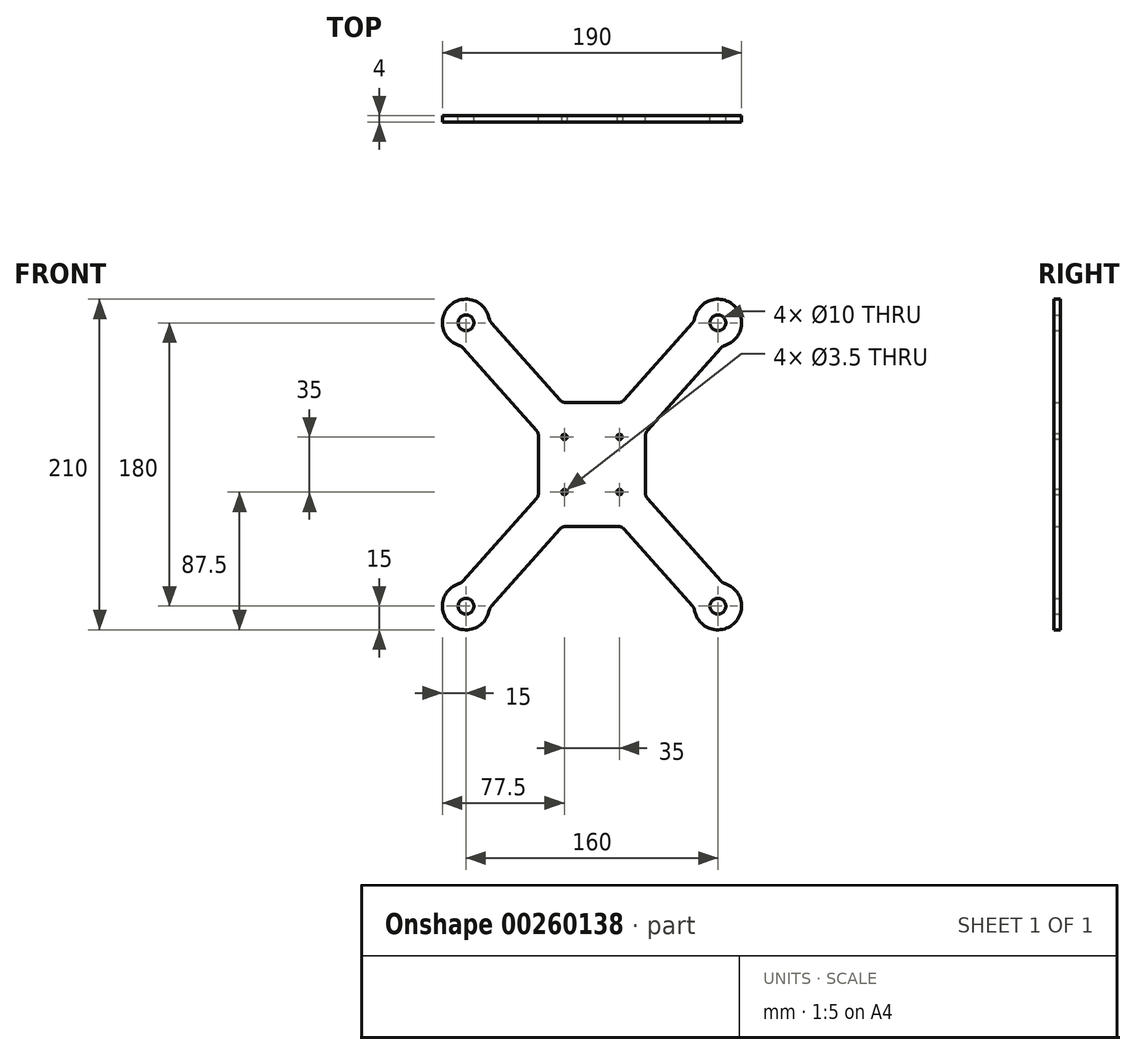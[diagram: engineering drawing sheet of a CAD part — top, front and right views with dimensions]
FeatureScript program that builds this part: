
annotation { "Feature Type Name" : "Feature", "Feature Type Description" : "" }
export const myFeature = defineFeature(function(context is Context, id is Id, definition is map)
    precondition{}
    {
        {
            var Q0;
            Q0=qCreatedBy(makeId("Front.planeOp"),FACE);
            var sketch = newSketch(context, id + "F0", { "sketchPlane" : qUnion([Q0])});
            skLineSegment(sketch, "E0", {"start": v(0, -138.98) * mm, "end": v(0, 18.06) * mm, "construction": true});
            skLineSegment(sketch, "E1.bottom", {"start": v(0, 90) * mm, "end": v(-80, 90) * mm, "construction": true});
            skLineSegment(sketch, "E1.top", {"start": v(0, -90) * mm, "end": v(-80, -90) * mm, "construction": true});
            skLineSegment(sketch, "E1.left", {"start": v(0, 90) * mm, "end": v(0, -90) * mm, "construction": true});
            skLineSegment(sketch, "E1.right", {"start": v(-80, 90) * mm, "end": v(-80, -90) * mm, "construction": true});
            skArc(sketch, "E2", {"start": v(-65.05, 91.25) * mm, "mid": v(-89.97, 101.21) * mm, "end": v(-82.99, 75.3) * mm});
            skArc(sketch, "E3", {"start": v(-82.99, -75.3) * mm, "mid": v(-89.97, -101.21) * mm, "end": v(-65.05, -91.25) * mm});
            skPoint(sketch, "E4", {"position": v(-80, 0) * mm});
            skLineSegment(sketch, "E5", {"start": v(-70.03, 78.79) * mm, "end": v(0, 0) * mm, "construction": true});
            skLineSegment(sketch, "E6", {"start": v(0, 0) * mm, "end": v(-80, -90) * mm, "construction": true});
            skLineSegment(sketch, "E7.0", {"start": v(-35.26, -21.6) * mm, "end": v(-82.99, -75.3) * mm});
            skLineSegment(sketch, "E7.1", {"start": v(-82.99, 75.3) * mm, "end": v(-35.26, 21.6) * mm});
            skLineSegment(sketch, "E8.0", {"start": v(-20.45, -41.07) * mm, "end": v(-65.05, -91.25) * mm});
            skLineSegment(sketch, "E8.1", {"start": v(-65.05, 91.25) * mm, "end": v(-20.45, 41.07) * mm});
            skLineSegment(sketch, "E9.trimOffspring", {"start": v(0, 90) * mm, "end": v(0, 152.4) * mm, "construction": true});
            skLineSegment(sketch, "E10.MirrorCS", {"start": v(65.05, 91.25) * mm, "end": v(20.45, 41.07) * mm});
            skArc(sketch, "E11.MirrorC", {"start": v(65.05, 91.25) * mm, "mid": v(89.97, 101.21) * mm, "end": v(82.99, 75.3) * mm});
            skLineSegment(sketch, "E12.MirrorCS", {"start": v(82.99, 75.3) * mm, "end": v(35.26, 21.6) * mm});
            skLineSegment(sketch, "E13.MirrorCS", {"start": v(35.26, -21.6) * mm, "end": v(82.99, -75.3) * mm});
            skArc(sketch, "E14.MirrorC", {"start": v(82.99, -75.3) * mm, "mid": v(89.97, -101.21) * mm, "end": v(65.05, -91.25) * mm});
            skLineSegment(sketch, "E15.MirrorCS", {"start": v(20.45, -41.07) * mm, "end": v(65.05, -91.25) * mm});
            skLineSegment(sketch, "E16.bottom", {"start": v(-16.72, 39.4) * mm, "end": v(16.72, 39.4) * mm});
            skLineSegment(sketch, "E16.top", {"start": v(-16.72, -39.4) * mm, "end": v(16.72, -39.4) * mm});
            skLineSegment(sketch, "E16.left", {"start": v(-34, 18.29) * mm, "end": v(-34, -18.29) * mm});
            skLineSegment(sketch, "E16.right", {"start": v(34, 18.29) * mm, "end": v(34, -18.29) * mm});
            skPoint(sketch, "E16.middle", {"position": v(0, 0) * mm});
            skPoint(sketch, "E17.newPointA", {"position": v(-16.06, 0) * mm});
            skArc(sketch, "E17.filletArc", {"start": v(-34, 18.29) * mm, "mid": v(-34.33, 20.06) * mm, "end": v(-35.26, 21.6) * mm});
            skArc(sketch, "E18.filletArc", {"start": v(-35.26, -21.6) * mm, "mid": v(-34.33, -20.06) * mm, "end": v(-34, -18.29) * mm});
            skPoint(sketch, "E19.newPointA", {"position": v(-35.02, 39.4) * mm});
            skPoint(sketch, "E19.newPointB", {"position": v(0, 18.06) * mm});
            skArc(sketch, "E19.filletArc", {"start": v(-20.45, 41.07) * mm, "mid": v(-18.76, 39.83) * mm, "end": v(-16.72, 39.4) * mm});
            skPoint(sketch, "E20.newPointA", {"position": v(35.02, 39.4) * mm});
            skArc(sketch, "E20.filletArc", {"start": v(16.72, 39.4) * mm, "mid": v(18.76, 39.83) * mm, "end": v(20.45, 41.07) * mm});
            skPoint(sketch, "E21.newPointB", {"position": v(16.06, 0) * mm});
            skArc(sketch, "E21.filletArc", {"start": v(35.26, 21.6) * mm, "mid": v(34.33, 20.06) * mm, "end": v(34, 18.29) * mm});
            skArc(sketch, "E22.filletArc", {"start": v(34, -18.29) * mm, "mid": v(34.33, -20.06) * mm, "end": v(35.26, -21.6) * mm});
            skPoint(sketch, "E23.newPointA", {"position": v(35.02, -39.4) * mm});
            skPoint(sketch, "E23.newPointB", {"position": v(0, -18.06) * mm});
            skArc(sketch, "E23.filletArc", {"start": v(20.45, -41.07) * mm, "mid": v(18.76, -39.83) * mm, "end": v(16.72, -39.4) * mm});
            skPoint(sketch, "E24.newPointB", {"position": v(-35.02, -39.4) * mm});
            skArc(sketch, "E24.filletArc", {"start": v(-16.72, -39.4) * mm, "mid": v(-18.76, -39.83) * mm, "end": v(-20.45, -41.07) * mm});
            skCircle(sketch, "E25", {"center": v(80, 90) * mm, "radius": 5 * mm});
            skCircle(sketch, "E26.MirrorC", {"center": v(80, -90) * mm, "radius": 5 * mm});
            skCircle(sketch, "E27.MirrorC", {"center": v(-80, -90) * mm, "radius": 5 * mm});
            skCircle(sketch, "E28.MirrorC", {"center": v(-80, 90) * mm, "radius": 5 * mm});
            skLineSegment(sketch, "E29", {"start": v(-80, -90) * mm, "end": v(-68.79, -99.97) * mm, "construction": true});
            skLineSegment(sketch, "E30", {"start": v(-80, -90) * mm, "end": v(-79.12, -104.97) * mm, "construction": true});
            skSolve(sketch);
        }
        {
            var Q0;
            Q0 = qSketchRegion(id + "F0", true);
            extrude(context, id + "F1", {"entities" : qUnion([Q0]), "depth" : 4 * mm});
        }
        {
            var Q0;
            Q0=makeQuery(id+"F1.opExtrude","CAP_FACE",FACE,{"disambiguationData":[OSD([sQuery(id+"F0.wireOp",EDGE,"E2"),sQuery(id+"F0.wireOp",EDGE,"E3"),sQuery(id+"F0.wireOp",EDGE,"E7.0"),sQuery(id+"F0.wireOp",EDGE,"E7.1"),sQuery(id+"F0.wireOp",EDGE,"E8.0"),sQuery(id+"F0.wireOp",EDGE,"E8.1"),sQuery(id+"F0.wireOp",EDGE,"E10.MirrorCS"),sQuery(id+"F0.wireOp",EDGE,"E11.MirrorC"),sQuery(id+"F0.wireOp",EDGE,"E12.MirrorCS"),sQuery(id+"F0.wireOp",EDGE,"E13.MirrorCS"),sQuery(id+"F0.wireOp",EDGE,"E14.MirrorC"),sQuery(id+"F0.wireOp",EDGE,"E15.MirrorCS"),sQuery(id+"F0.wireOp",EDGE,"E16.bottom"),sQuery(id+"F0.wireOp",EDGE,"E16.top"),sQuery(id+"F0.wireOp",EDGE,"E16.left"),sQuery(id+"F0.wireOp",EDGE,"E16.right"),sQuery(id+"F0.wireOp",EDGE,"E17.filletArc"),sQuery(id+"F0.wireOp",EDGE,"E18.filletArc"),sQuery(id+"F0.wireOp",EDGE,"E19.filletArc"),sQuery(id+"F0.wireOp",EDGE,"E20.filletArc"),sQuery(id+"F0.wireOp",EDGE,"E21.filletArc"),sQuery(id+"F0.wireOp",EDGE,"E22.filletArc"),sQuery(id+"F0.wireOp",EDGE,"E23.filletArc"),sQuery(id+"F0.wireOp",EDGE,"E24.filletArc"),sQuery(id+"F0.wireOp",EDGE,"E25"),sQuery(id+"F0.wireOp",EDGE,"E26.MirrorC"),sQuery(id+"F0.wireOp",EDGE,"E27.MirrorC"),sQuery(id+"F0.wireOp",EDGE,"E28.MirrorC")])],"isStart":false});
            var sketch = newSketch(context, id + "F4", { "sketchPlane" : qUnion([Q0])});
            skLineSegment(sketch, "E31.bottom", {"start": v(17.5, 17.5) * mm, "end": v(-17.5, 17.5) * mm});
            skLineSegment(sketch, "E31.top", {"start": v(17.5, -17.5) * mm, "end": v(-17.5, -17.5) * mm});
            skLineSegment(sketch, "E31.left", {"start": v(17.5, 17.5) * mm, "end": v(17.5, -17.5) * mm});
            skLineSegment(sketch, "E31.right", {"start": v(-17.5, 17.5) * mm, "end": v(-17.5, -17.5) * mm});
            skPoint(sketch, "E31.middle", {"position": v(0, 0) * mm});
            skCircle(sketch, "E32", {"center": v(-17.5, 17.5) * mm, "radius": 1.75 * mm});
            skCircle(sketch, "E33", {"center": v(-17.5, -17.5) * mm, "radius": 1.75 * mm});
            skCircle(sketch, "E34", {"center": v(17.5, -17.5) * mm, "radius": 1.75 * mm});
            skCircle(sketch, "E35", {"center": v(17.5, 17.5) * mm, "radius": 1.75 * mm});
            skSolve(sketch);
        }
        {
            var Q0;
            {var subQ0=sQuery(id+"F4.wireOp",EDGE,"E31.left");var subQ1=sQuery(id+"F4.wireOp",EDGE,"E31.bottom");var subQ2=makeQuery(id+"F4.imprint","INTERSECT",VERTEX,{"derivedFrom":[subQ1,subQ0]});Q0=makeQuery(id+"F4.imprint","IMPRINT",FACE,{"disambiguationData":[TD([[makeQuery(id+"F4.imprint","IMPRINT",EDGE,{"disambiguationData":[TD([[subQ2,-1.0]])],"derivedFrom":subQ1}),-1.0]])]});}
            var Q1;
            {var subQ0=sQuery(id+"F4.wireOp",EDGE,"E31.right");var subQ1=sQuery(id+"F4.wireOp",EDGE,"E31.bottom");var subQ2=makeQuery(id+"F4.imprint","INTERSECT",VERTEX,{"derivedFrom":[subQ1,subQ0]});Q1=makeQuery(id+"F4.imprint","IMPRINT",FACE,{"disambiguationData":[TD([[makeQuery(id+"F4.imprint","IMPRINT",EDGE,{"disambiguationData":[TD([[subQ2,1.0]])],"derivedFrom":subQ1}),-1.0]])]});}
            var Q2;
            {var subQ0=sQuery(id+"F4.wireOp",EDGE,"E31.right");var subQ1=sQuery(id+"F4.wireOp",EDGE,"E31.bottom");var subQ2=makeQuery(id+"F4.imprint","INTERSECT",VERTEX,{"derivedFrom":[subQ1,subQ0]});Q2=makeQuery(id+"F4.imprint","IMPRINT",FACE,{"disambiguationData":[TD([[makeQuery(id+"F4.imprint","IMPRINT",EDGE,{"disambiguationData":[TD([[subQ2,1.0]])],"derivedFrom":subQ1}),1.0]])]});}
            var Q3;
            {var subQ0=sQuery(id+"F4.wireOp",EDGE,"E31.left");var subQ1=sQuery(id+"F4.wireOp",EDGE,"E31.bottom");var subQ2=makeQuery(id+"F4.imprint","INTERSECT",VERTEX,{"derivedFrom":[subQ1,subQ0]});Q3=makeQuery(id+"F4.imprint","IMPRINT",FACE,{"disambiguationData":[TD([[makeQuery(id+"F4.imprint","IMPRINT",EDGE,{"disambiguationData":[TD([[subQ2,-1.0]])],"derivedFrom":subQ1}),1.0]])]});}
            var Q4;
            {var subQ0=sQuery(id+"F4.wireOp",EDGE,"E31.right");var subQ1=sQuery(id+"F4.wireOp",EDGE,"E31.top");var subQ2=makeQuery(id+"F4.imprint","INTERSECT",VERTEX,{"derivedFrom":[subQ1,subQ0]});Q4=makeQuery(id+"F4.imprint","IMPRINT",FACE,{"disambiguationData":[TD([[makeQuery(id+"F4.imprint","IMPRINT",EDGE,{"disambiguationData":[TD([[subQ2,1.0]])],"derivedFrom":subQ1}),-1.0]])]});}
            var Q5;
            {var subQ0=sQuery(id+"F4.wireOp",EDGE,"E31.right");var subQ1=sQuery(id+"F4.wireOp",EDGE,"E31.top");var subQ2=makeQuery(id+"F4.imprint","INTERSECT",VERTEX,{"derivedFrom":[subQ1,subQ0]});Q5=makeQuery(id+"F4.imprint","IMPRINT",FACE,{"disambiguationData":[TD([[makeQuery(id+"F4.imprint","IMPRINT",EDGE,{"disambiguationData":[TD([[subQ2,1.0]])],"derivedFrom":subQ1}),1.0]])]});}
            var Q6;
            {var subQ0=sQuery(id+"F4.wireOp",EDGE,"E31.left");var subQ1=sQuery(id+"F4.wireOp",EDGE,"E31.top");var subQ2=makeQuery(id+"F4.imprint","INTERSECT",VERTEX,{"derivedFrom":[subQ1,subQ0]});Q6=makeQuery(id+"F4.imprint","IMPRINT",FACE,{"disambiguationData":[TD([[makeQuery(id+"F4.imprint","IMPRINT",EDGE,{"disambiguationData":[TD([[subQ2,-1.0]])],"derivedFrom":subQ1}),-1.0]])]});}
            var Q7;
            {var subQ0=sQuery(id+"F4.wireOp",EDGE,"E31.left");var subQ1=sQuery(id+"F4.wireOp",EDGE,"E31.top");var subQ2=makeQuery(id+"F4.imprint","INTERSECT",VERTEX,{"derivedFrom":[subQ1,subQ0]});Q7=makeQuery(id+"F4.imprint","IMPRINT",FACE,{"disambiguationData":[TD([[makeQuery(id+"F4.imprint","IMPRINT",EDGE,{"disambiguationData":[TD([[subQ2,-1.0]])],"derivedFrom":subQ1}),1.0]])]});}
            extrude(context, id + "F2", {"entities" : qUnion([Q0, Q1, Q2, Q3, Q4, Q5, Q6, Q7]), "operationType" : NewBodyOperationType.REMOVE, "oppositeDirection" : true, "depth" : 25 * mm});
        }
        {
            var Q0;
            Q0=makeQuery(id+"F1.opExtrude","SWEPT_EDGE",EDGE,{"disambiguationData":[OSD([sQuery(id+"F0.wireOp",EDGE,"E13.MirrorCS"),sQuery(id+"F0.wireOp",EDGE,"E14.MirrorC")])]});
            var Q1;
            Q1=makeQuery(id+"F1.opExtrude","SWEPT_EDGE",EDGE,{"disambiguationData":[OSD([sQuery(id+"F0.wireOp",EDGE,"E14.MirrorC"),sQuery(id+"F0.wireOp",EDGE,"E15.MirrorCS")])]});
            var Q2;
            Q2=makeQuery(id+"F1.opExtrude","SWEPT_EDGE",EDGE,{"disambiguationData":[OSD([sQuery(id+"F0.wireOp",EDGE,"E3"),sQuery(id+"F0.wireOp",EDGE,"E7.0")])]});
            var Q3;
            Q3=makeQuery(id+"F1.opExtrude","SWEPT_EDGE",EDGE,{"disambiguationData":[OSD([sQuery(id+"F0.wireOp",EDGE,"E3"),sQuery(id+"F0.wireOp",EDGE,"E8.0")])]});
            var Q4;
            Q4=makeQuery(id+"F1.opExtrude","SWEPT_EDGE",EDGE,{"disambiguationData":[OSD([sQuery(id+"F0.wireOp",EDGE,"E10.MirrorCS"),sQuery(id+"F0.wireOp",EDGE,"E11.MirrorC")])]});
            var Q5;
            Q5=makeQuery(id+"F1.opExtrude","SWEPT_EDGE",EDGE,{"disambiguationData":[OSD([sQuery(id+"F0.wireOp",EDGE,"E11.MirrorC"),sQuery(id+"F0.wireOp",EDGE,"E12.MirrorCS")])]});
            var Q6;
            Q6=makeQuery(id+"F1.opExtrude","SWEPT_EDGE",EDGE,{"disambiguationData":[OSD([sQuery(id+"F0.wireOp",EDGE,"E2"),sQuery(id+"F0.wireOp",EDGE,"E7.1")])]});
            var Q7;
            Q7=makeQuery(id+"F1.opExtrude","SWEPT_EDGE",EDGE,{"disambiguationData":[OSD([sQuery(id+"F0.wireOp",EDGE,"E2"),sQuery(id+"F0.wireOp",EDGE,"E8.1")])]});
            fillet(context, id + "F3", {"entities" : qUnion([Q0, Q1, Q2, Q3, Q4, Q5, Q6, Q7]), "radius" : 6 * mm, "tangentPropagation" : true, "allowEdgeOverflow" : false});
        }
    });
